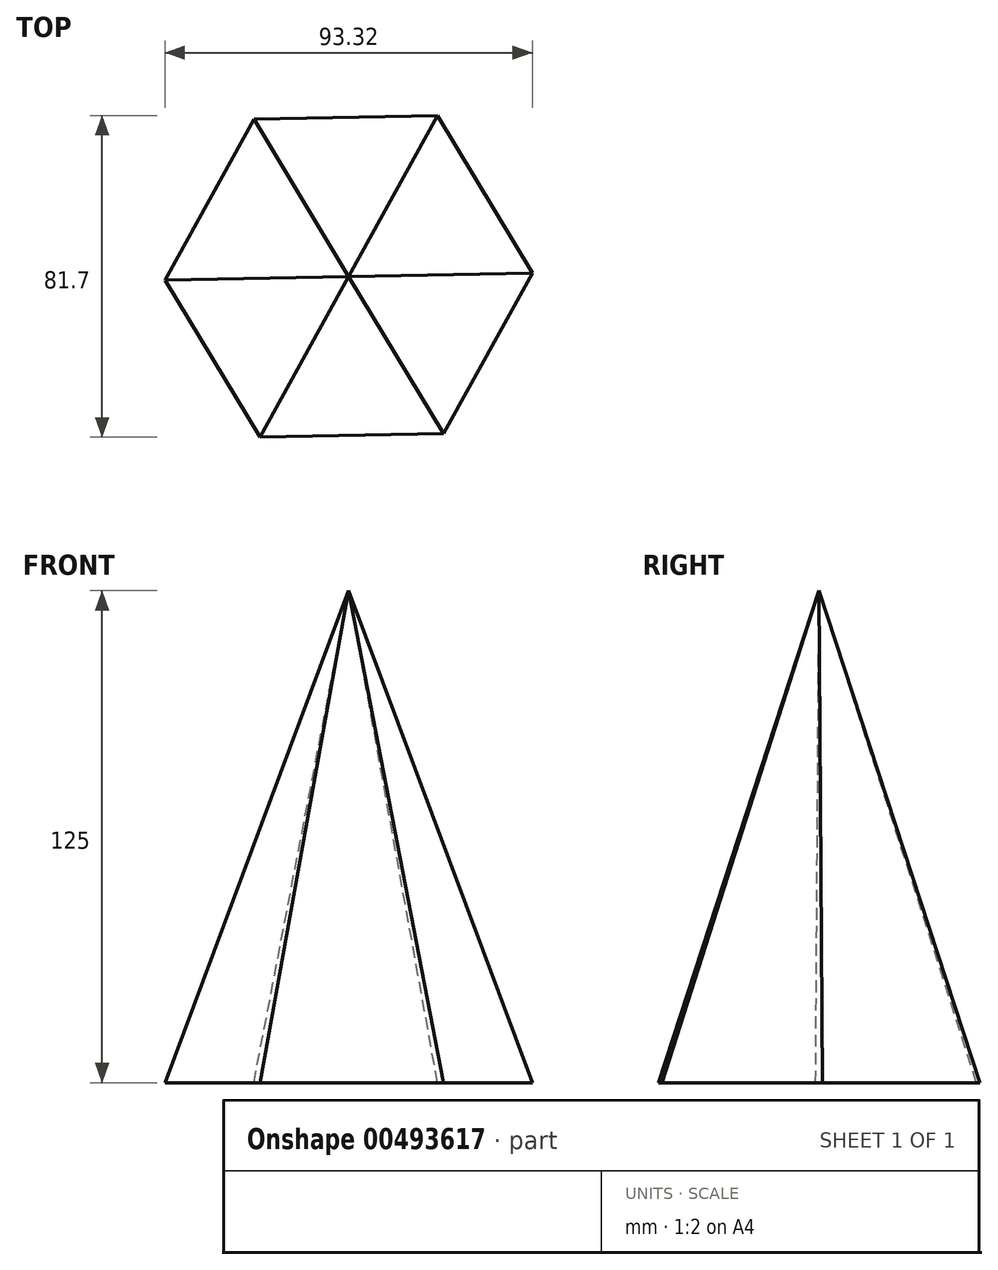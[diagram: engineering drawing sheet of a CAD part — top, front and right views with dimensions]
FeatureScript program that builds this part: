
annotation { "Feature Type Name" : "Feature", "Feature Type Description" : "" }
export const myFeature = defineFeature(function(context is Context, id is Id, definition is map)
    precondition{}
    {
        {
            var Q0;
            Q0=qCreatedBy(makeId("Top.planeOp"),FACE);
            var sketch = newSketch(context, id + "F0", { "sketchPlane" : qUnion([Q0])});
            skCircle(sketch, "E0.cCircle", {"center": v(0, 0) * mm, "radius": 46.67 * mm, "construction": true});
            skLineSegment(sketch, "E0.0", {"start": v(24.1, -39.97) * mm, "end": v(-22.56, -40.85) * mm});
            skLineSegment(sketch, "E0.1", {"start": v(-22.56, -40.85) * mm, "end": v(-46.66, -0.89) * mm});
            skLineSegment(sketch, "E0.2", {"start": v(-46.66, -0.89) * mm, "end": v(-24.1, 39.97) * mm});
            skLineSegment(sketch, "E0.3", {"start": v(-24.1, 39.97) * mm, "end": v(22.56, 40.85) * mm});
            skLineSegment(sketch, "E0.4", {"start": v(22.56, 40.85) * mm, "end": v(46.66, 0.89) * mm});
            skLineSegment(sketch, "E0.5", {"start": v(46.66, 0.89) * mm, "end": v(24.1, -39.97) * mm});
            skSolve(sketch);
        }
        {
            var Q0;
            Q0=qCreatedBy(makeId("Top.planeOp"),FACE);
            cPlane(context, id + "F1", {"entities" : qUnion([Q0]), "cplaneType" : CPlaneType.OFFSET, "offset" : 125 * mm, "width" : 150 * mm, "height" : 150 * mm});
        }
        {
            var Q0;
            Q0=qCreatedBy(id+"F1.planeOp",FACE);
            var sketch = newSketch(context, id + "F2", { "sketchPlane" : qUnion([Q0])});
            skPoint(sketch, "E1", {"position": v(0, 0) * mm});
            skSolve(sketch);
        }
        {
            var Q0;
            Q0=makeQuery(id+"F0.imprint","IMPRINT",FACE,{"disambiguationData":[TD([[makeQuery(id+"F0.imprint","IMPRINT",EDGE,{"derivedFrom":sQuery(id+"F0.wireOp",EDGE,"E0.0")}),-1.0]])]});
            var Q1;
            Q1=sQuery(id+"F2.wireOp",VERTEX,"E1");
            loft(context, id + "F3", {"sheetProfilesArray" : [{ "sheetProfileEntities" : qUnion([Q0]) }, { "sheetProfileEntities" : qUnion([Q1]) }]});
        }
    });
